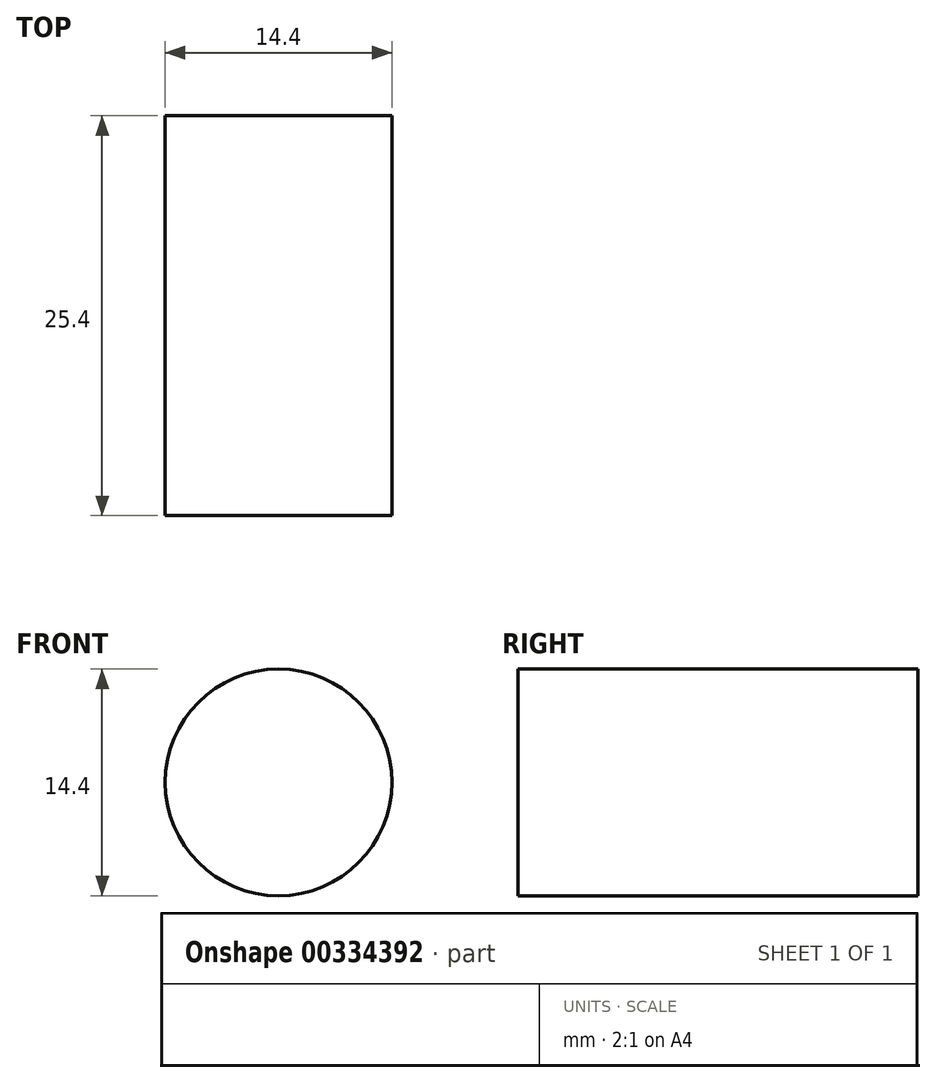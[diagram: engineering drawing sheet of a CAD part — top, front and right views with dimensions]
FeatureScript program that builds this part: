
annotation { "Feature Type Name" : "Feature", "Feature Type Description" : "" }
export const myFeature = defineFeature(function(context is Context, id is Id, definition is map)
    precondition{}
    {
        {
            var Q0;
            Q0=qCreatedBy(makeId("Front.planeOp"),FACE);
            var sketch = newSketch(context, id + "F0", { "sketchPlane" : qUnion([Q0])});
            skCircle(sketch, "E0", {"center": v(0, 0) * mm, "radius": 15.9 * mm});
            skSolve(sketch);
        }
        {
            var Q0;
            Q0=makeQuery(id+"F0.imprint","IMPRINT",FACE,{"disambiguationData":[TD([[makeQuery(id+"F0.imprint","IMPRINT",EDGE,{"derivedFrom":sQuery(id+"F0.wireOp",EDGE,"E0")}),1.0]])]});
            var sketch = newSketch(context, id + "F1", { "sketchPlane" : qUnion([Q0])});
            skCircle(sketch, "E1", {"center": v(0, 0) * mm, "radius": 7.2 * mm});
            skCircle(sketch, "E2", {"center": v(1.46, 7.72) * mm, "radius": 10.28 * mm});
            skSolve(sketch);
        }
        {
            var Q0;
            Q0=makeQuery(id+"F0.imprint","IMPRINT",FACE,{"disambiguationData":[TD([[makeQuery(id+"F0.imprint","IMPRINT",EDGE,{"derivedFrom":sQuery(id+"F0.wireOp",EDGE,"E0")}),1.0]])]});
            extrude(context, id + "F2", {"entities" : qUnion([Q0]), "depth" : 25.4 * mm});
        }
        {
            var Q0;
            Q0=makeQuery(id+"F2.opExtrude","CAP_FACE",FACE,{"disambiguationData":[OSD([sQuery(id+"F0.wireOp",EDGE,"E0")])],"isStart":false});
            extrude(context, id + "F3", {"entities" : qUnion([Q0]), "operationType" : NewBodyOperationType.REMOVE, "oppositeDirection" : true, "depth" : 25.4 * mm});
        }
        {
            var Q0;
            Q0=sQuery(id+"F1.wireOp",EDGE,"E1");
            extrude(context, id + "F4", {"bodyType" : ToolBodyType.SURFACE, "surfaceEntities" : qUnion([Q0]), "depth" : 25.4 * mm});
        }
    });
